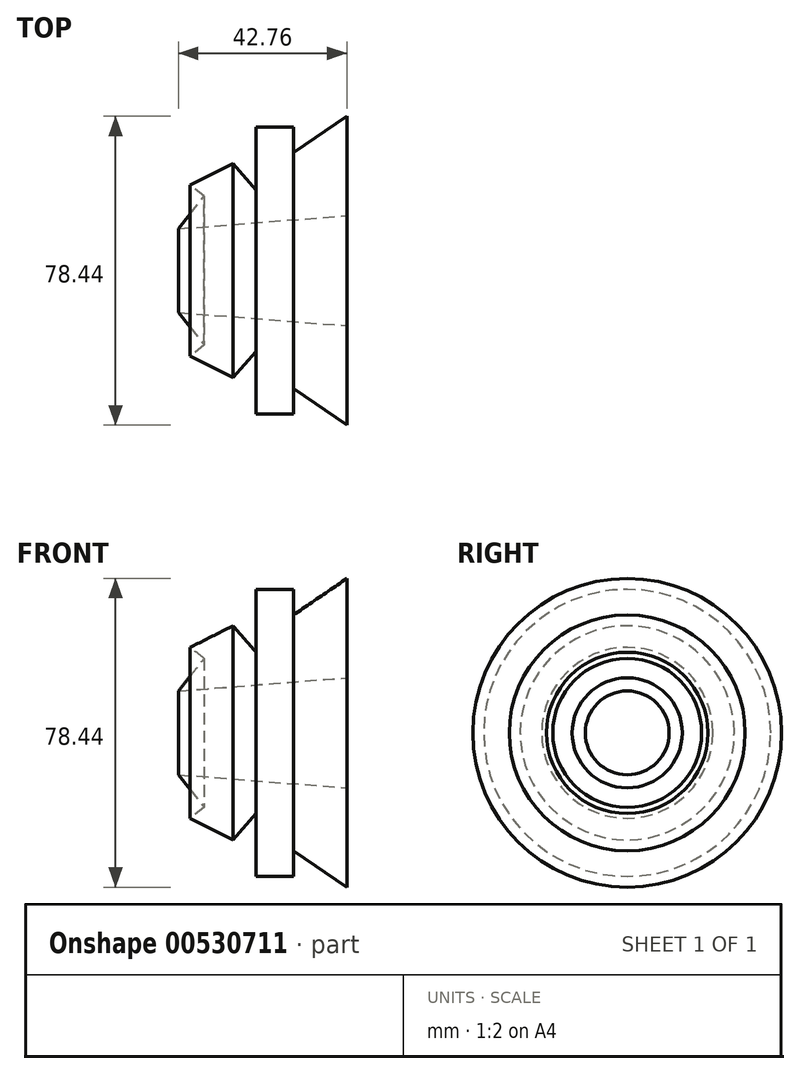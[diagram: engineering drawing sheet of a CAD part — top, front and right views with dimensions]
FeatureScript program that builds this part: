
annotation { "Feature Type Name" : "Feature", "Feature Type Description" : "" }
export const myFeature = defineFeature(function(context is Context, id is Id, definition is map)
    precondition{}
    {
        {
            var Q0;
            Q0=qCreatedBy(makeId("Front.planeOp"),FACE);
            var sketch = newSketch(context, id + "F0", { "sketchPlane" : qUnion([Q0])});
            skLineSegment(sketch, "E0", {"start": v(0, 0) * mm, "end": v(-85.33, 0) * mm});
            skLineSegment(sketch, "E1", {"start": v(0, 14) * mm, "end": v(-42.76, 10.64) * mm});
            skLineSegment(sketch, "E2", {"start": v(-42.76, 10.64) * mm, "end": v(-36.26, 18.92) * mm});
            skLineSegment(sketch, "E3", {"start": v(-36.26, 18.92) * mm, "end": v(-39.82, 21.72) * mm});
            skLineSegment(sketch, "E4", {"start": v(-39.82, 21.72) * mm, "end": v(-28.97, 27.2) * mm});
            skLineSegment(sketch, "E5", {"start": v(-28.97, 27.2) * mm, "end": v(-23.06, 20.5) * mm});
            skLineSegment(sketch, "E6", {"start": v(-23.06, 20.5) * mm, "end": v(-23.06, 36.46) * mm});
            skLineSegment(sketch, "E7", {"start": v(-23.06, 36.46) * mm, "end": v(-13.6, 36.46) * mm});
            skLineSegment(sketch, "E8", {"start": v(-13.6, 36.46) * mm, "end": v(-13.6, 29.95) * mm});
            skLineSegment(sketch, "E9", {"start": v(-13.6, 29.95) * mm, "end": v(0, 39.22) * mm});
            skSolve(sketch);
        }
        {
            var Q0;
            Q0=sQuery(id+"F0.wireOp",EDGE,"E5");
            var Q1;
            Q1=sQuery(id+"F0.wireOp",EDGE,"E6");
            var Q2;
            Q2=sQuery(id+"F0.wireOp",EDGE,"E7");
            var Q3;
            Q3=sQuery(id+"F0.wireOp",EDGE,"E2");
            var Q4;
            Q4=sQuery(id+"F0.wireOp",EDGE,"E1");
            var Q5;
            Q5=sQuery(id+"F0.wireOp",EDGE,"E4");
            var Q6;
            Q6=sQuery(id+"F0.wireOp",EDGE,"E8");
            var Q7;
            Q7=sQuery(id+"F0.wireOp",EDGE,"E3");
            var Q8;
            Q8=sQuery(id+"F0.wireOp",EDGE,"E9");
            var Q9;
            Q9=sQuery(id+"F0.wireOp",EDGE,"E0");
            revolve(context, id + "F1", {"bodyType" : ToolBodyType.SURFACE, "surfaceEntities" : qUnion([Q0, Q1, Q2, Q3, Q4, Q5, Q6, Q7, Q8]), "axis" : qUnion([Q9]), "revolveType" : RevolveType.FULL});
        }
    });
